# Revit family: FP-Revit20-en-WB30S_VB30S_WarmingDrawer_VacuumSealDrawer-0-90005524A-US-CA
name_source: partatom
category: Specialty Equipment
units: mm (PartAtom-declared; Revit-internal decimal feet)

## family parameters
Always vertical = Yes
Cut with Voids When Loaded = Yes
OmniClass Number = 23.40.40.14.17.31
OmniClass Title = Small Specialized Cooking Equipment
Part Type = Normal
Room Calculation Point = No
Round Connector Dimension = Use Diameter
Shared = No
Work Plane-Based = No

## types (10) — shared parameters
Cavity - Depth = 580 mm  [stored 1.90289 ft]
Cavity - Height = 271 mm  [stored 0.889108 ft]
Cavity - Width = 724 mm  [stored 2.37533 ft]
Connector Description - Electrical = 120 V, 60 Hz, 10 A circuit
Manufacturer = Fisher & Paykel Appliances
Material - Body = Fisher & Paykel - Grey
Material - Clearance Required = Fisher & Paykel - Clearance Required
Opening - Height = 271 mm  [stored 0.889108 ft]
Opening - Width = 762 mm  [stored 2.5 ft]
Product - Height = 271 mm  [stored 0.889108 ft]
Product - Width = 758 mm  [stored 2.48688 ft]
URL = www.fisherpaykel.com
Visibility - Minimal/Contemporary/Professional/Integrated = Yes
zero-valued in all types: Default Elevation

## per-type parameters (varying)
| type | Control Panel - Depth | Description | Material - Front | Material - Structure | Opening - Depth | Panel - Material | Product - Depth (not incl handles) | Style - Chassis | Style - Front | Type Comments | Visibiity - Anti Tip Brackets Rear | Visibility - Integrated |
| WB30SPEX3 | 24 mm  [stored 0.0787402 ft] | 30" Warming Drawer | Fisher & Paykel - Stainless Steel | Fisher & Paykel - Stainless Steel | 24 mm  [stored 0.0787402 ft] | <By Category> | 567 mm  [stored 1.86024 ft] | 30in-76cm Drawer Chassis : Chassis Warmer - Professional | 30in-76cm Drawer Fronts : 30in Front Professional | Professional, Stainless | No | No |
| WB30SMB3 | 20 mm  [stored 0.0656168 ft] | 30" Warming Drawer | Fisher & Paykel - Glass, Black | Fisher & Paykel - Black | 20 mm  [stored 0.0656168 ft] | <By Category> | 567 mm  [stored 1.86024 ft] | 30in-76cm Drawer Chassis : Chassis Warmer - Minimal/Contemporary | 30in-76cm Drawer Fronts : 30in Front (Black) No Handle | Minimal, Black | No | No |
| WB30SCX3 | 20 mm  [stored 0.0656168 ft] | 30" Warming Drawer | Fisher & Paykel - Glass, Brushed | Fisher & Paykel - Black | 20 mm  [stored 0.0656168 ft] | <By Category> | 567 mm  [stored 1.86024 ft] | 30in-76cm Drawer Chassis : Chassis Warmer - Minimal/Contemporary | 30in-76cm Drawer Fronts : 30in Front (Contemporary) No Handle | Contemporary, Stainless | No | No |
| WB30SDEI3 | 19 mm  [stored 0.062336 ft] | 30" Warming Drawer | <By Category> | Fisher & Paykel - Stainless Steel | 19 mm  [stored 0.062336 ft] | Ash | 566 mm | 30in-76cm Drawer Chassis : Chassis Warmer - Integrated | 30in-76cm Drawer Fronts : 30in Front (Integrated) | Integrated | No | Yes |
| WB30SMG3 | 20 mm  [stored 0.0656168 ft] | 30" Warming Drawer | Fisher & Paykel - Glass, Grey | Fisher & Paykel - Black | 20 mm  [stored 0.0656168 ft] | <By Category> | 567 mm  [stored 1.86024 ft] | 30in-76cm Drawer Chassis : Chassis Warmer - Minimal/Contemporary | 30in-76cm Drawer Fronts : 30in Front (Grey) No Handle | Minimal, Grey | No | No |
| VB30SCX3 | 20 mm  [stored 0.0656168 ft] | 30" Vacuum Drawer | Fisher & Paykel - Glass, Brushed | Fisher & Paykel - Black | 20 mm  [stored 0.0656168 ft] | <By Category> | 573 mm | 30in-76cm Drawer Chassis : Chassis Vacuum - Minimal/Contemporary | 30in-76cm Drawer Fronts : 30in Front (Contemporary) No Handle | Contemporary, Stainless | Yes | No |
| VB30SDEI3 | 19 mm  [stored 0.062336 ft] | 30" Vacum Drawer | <By Category> | Fisher & Paykel - Stainless Steel | 19 mm  [stored 0.062336 ft] | Ash | 573 mm | 30in-76cm Drawer Chassis : Chassis Vacuum - Integrated | 30in-76cm Drawer Fronts : 30in Front (Integrated) | Integrated | Yes | Yes |
| VB30SMB3 | 20 mm  [stored 0.0656168 ft] | 30" Vacum Drawer | Fisher & Paykel - Glass, Black | Fisher & Paykel - Black | 20 mm  [stored 0.0656168 ft] | <By Category> | 573 mm | 30in-76cm Drawer Chassis : Chassis Vacuum - Minimal/Contemporary | 30in-76cm Drawer Fronts : 30in Front (Black) No Handle | Minimal, Black | No | No |
| VB30SMG3 | 20 mm  [stored 0.0656168 ft] | 30" Vacuum Drawer | Fisher & Paykel - Glass, Grey | Fisher & Paykel - Black | 20 mm  [stored 0.0656168 ft] | <By Category> | 573 mm | 30in-76cm Drawer Chassis : Chassis Vacuum - Minimal/Contemporary | 30in-76cm Drawer Fronts : 30in Front (Grey) No Handle | Minimal, Grey | Yes | No |
| VB30SPEX3 | 24 mm  [stored 0.0787402 ft] | 30" Vacuum Drawer | Fisher & Paykel - Stainless Steel | Fisher & Paykel - Stainless Steel | 24 mm  [stored 0.0787402 ft] | <By Category> | 573 mm | 30in-76cm Drawer Chassis : Chassis Vacuum - Professional | 30in-76cm Drawer Fronts : 30in Front Professional | Professional, Stainless | Yes | No |

note: column(s) folded — value = type name in every type: Model

note: [stored X ft] marks values corroborated as IEEE doubles in the binary element streams (Revit-internal decimal feet)

## geometry (parser evidence)
native form markers: Sweep x12
no freeform markers — native parametric forms only
